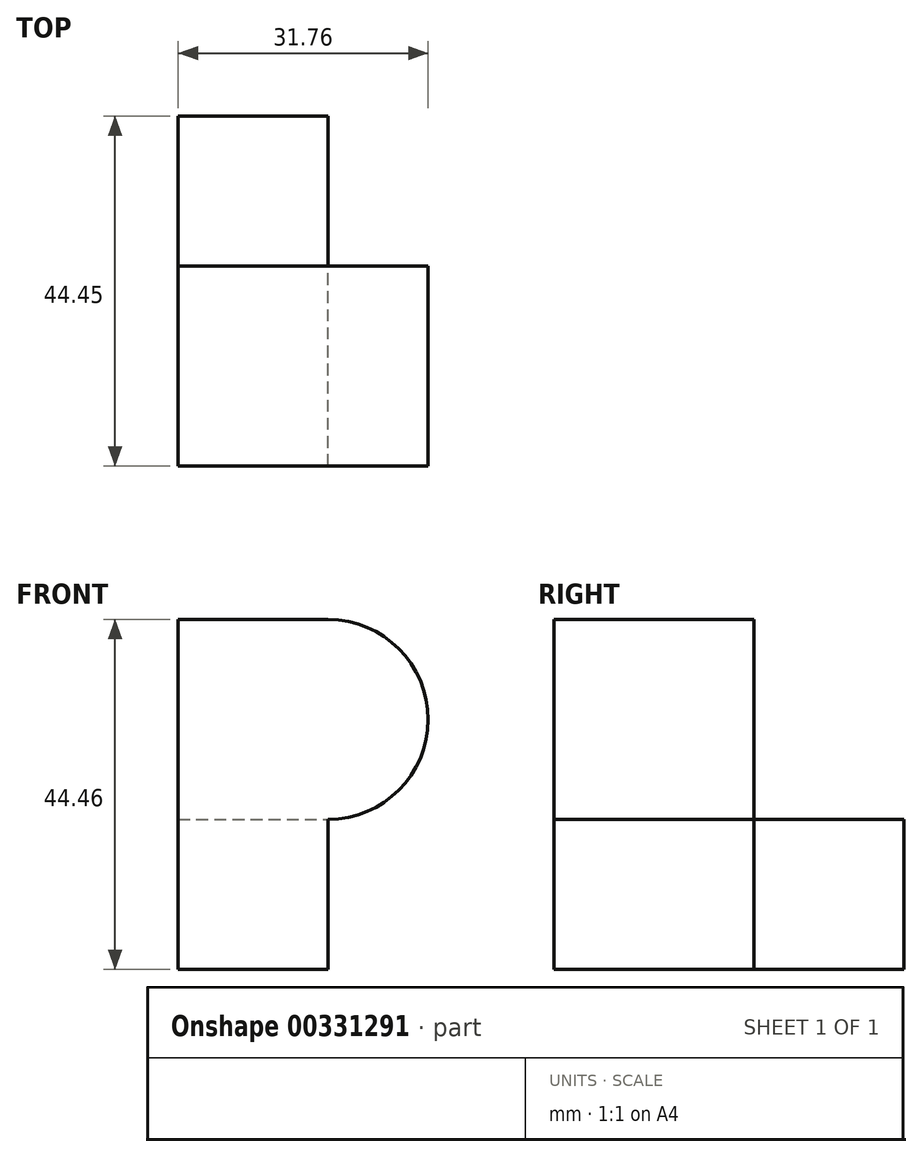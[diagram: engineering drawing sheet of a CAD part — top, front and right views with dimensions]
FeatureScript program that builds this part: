
annotation { "Feature Type Name" : "Feature", "Feature Type Description" : "" }
export const myFeature = defineFeature(function(context is Context, id is Id, definition is map)
    precondition{}
    {
        {
            var Q0;
            Q0=qCreatedBy(makeId("Front.planeOp"),FACE);
            var sketch = newSketch(context, id + "F0", { "sketchPlane" : qUnion([Q0])});
            skLineSegment(sketch, "E0.bottom", {"start": v(9.52, -22.23) * mm, "end": v(-9.52, -22.23) * mm});
            skLineSegment(sketch, "E0.top", {"start": v(9.52, 22.23) * mm, "end": v(-9.52, 22.23) * mm});
            skLineSegment(sketch, "E0.left", {"start": v(9.52, -22.23) * mm, "end": v(9.52, -3.18) * mm});
            skLineSegment(sketch, "E0.right", {"start": v(-9.52, -22.23) * mm, "end": v(-9.52, 22.23) * mm});
            skPoint(sketch, "E0.middle", {"position": v(0, 0) * mm});
            skArc(sketch, "E1", {"start": v(9.52, -3.18) * mm, "mid": v(22.22, 9.53) * mm, "end": v(9.52, 22.23) * mm});
            skLineSegment(sketch, "E2.trimOffspring", {"start": v(9.52, 22.23) * mm, "end": v(9.52, 22.23) * mm});
            skSolve(sketch);
        }
        {
            var Q0;
            Q0=makeQuery(id+"F0.imprint","IMPRINT",FACE,{"disambiguationData":[TD([[makeQuery(id+"F0.imprint","IMPRINT",EDGE,{"derivedFrom":sQuery(id+"F0.wireOp",EDGE,"E0.bottom")}),-1.0]])]});
            extrude(context, id + "F1", {"entities" : qUnion([Q0]), "depth" : 25.4 * mm});
        }
        {
            var Q0;
            Q0=makeQuery(id+"F1.opExtrude","SWEPT_FACE",FACE,{"disambiguationData":[OSD([sQuery(id+"F0.wireOp",EDGE,"E0.left")])]});
            var sketch = newSketch(context, id + "F2", { "sketchPlane" : qUnion([Q0])});
            skLineSegment(sketch, "E3.bottom", {"start": v(0, -3.18) * mm, "end": v(19.05, -3.18) * mm});
            skLineSegment(sketch, "E3.top", {"start": v(0, -22.23) * mm, "end": v(19.05, -22.23) * mm});
            skLineSegment(sketch, "E3.left", {"start": v(0, -3.18) * mm, "end": v(0, -22.23) * mm});
            skLineSegment(sketch, "E3.right", {"start": v(19.05, -3.18) * mm, "end": v(19.05, -22.23) * mm});
            skSolve(sketch);
        }
        {
            var Q0;
            Q0=makeQuery(id+"F2.imprint","IMPRINT",FACE,{"disambiguationData":[TD([[makeQuery(id+"F2.imprint","IMPRINT",EDGE,{"derivedFrom":sQuery(id+"F2.wireOp",EDGE,"E3.bottom")}),-1.0]])]});
            extrude(context, id + "F3", {"entities" : qUnion([Q0]), "oppositeDirection" : true, "depth" : 19.05 * mm});
        }
    });
